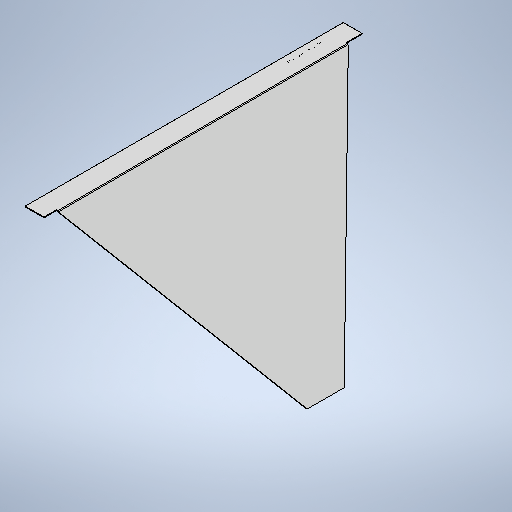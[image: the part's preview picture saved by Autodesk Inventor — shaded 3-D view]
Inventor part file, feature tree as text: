
AUTODESK INVENTOR PART (.ipt)
format: ipt  version: 2025 (Build 290162010, 162A)  size: 438,784 bytes
history: native  units: mm
features: other x4, sketch x4, sheet_metal_op x3, extrude x2
ambient origin geometry x8: Origin, YZ Plane, XZ Plane, XY Plane, X Axis, Y Axis, Z Axis, Center Point
bodies: Solid1 (feature_tree)
feature tree (13):
  sheet_metal_op  "Contour Flange1"
  extrude  "Extrusion6"  Depth=4.0mm
  extrude  "Extrusion7"  Depth=8.0mm
  other  "Mark2"
  other  "A-Side Definition"
  sketch  "Sketch1"  dims[d6=4.0mm d7=4.0mm]
  other  "Plate1"
  sheet_metal_op  "Bend1"
  sheet_metal_op  "Corner1"
  sketch  "Sketch9"  dims[d8=2.0mm d9=8.0mm]
  sketch  "Sketch10"  dims[d10=6.0mm]
  sketch  "Sketch16"  dims[d11=1536.0mm d12=6.0mm d13=4.0mm d14=16.0mm d15=4.0mm d16=6.0mm d61=88.0mm d62=230.0mm d63=1150.0mm d64=6.0mm d65=800.0mm d66=60.0mm d68=10.0mm d69=0.0mm d71=4.0mm d72=0.0mm d90=50.0mm d93=196.0mm d94=66.0mm d95=6.0mm d96=87.0mm d97=3.0mm]
  other  "Definition1"
